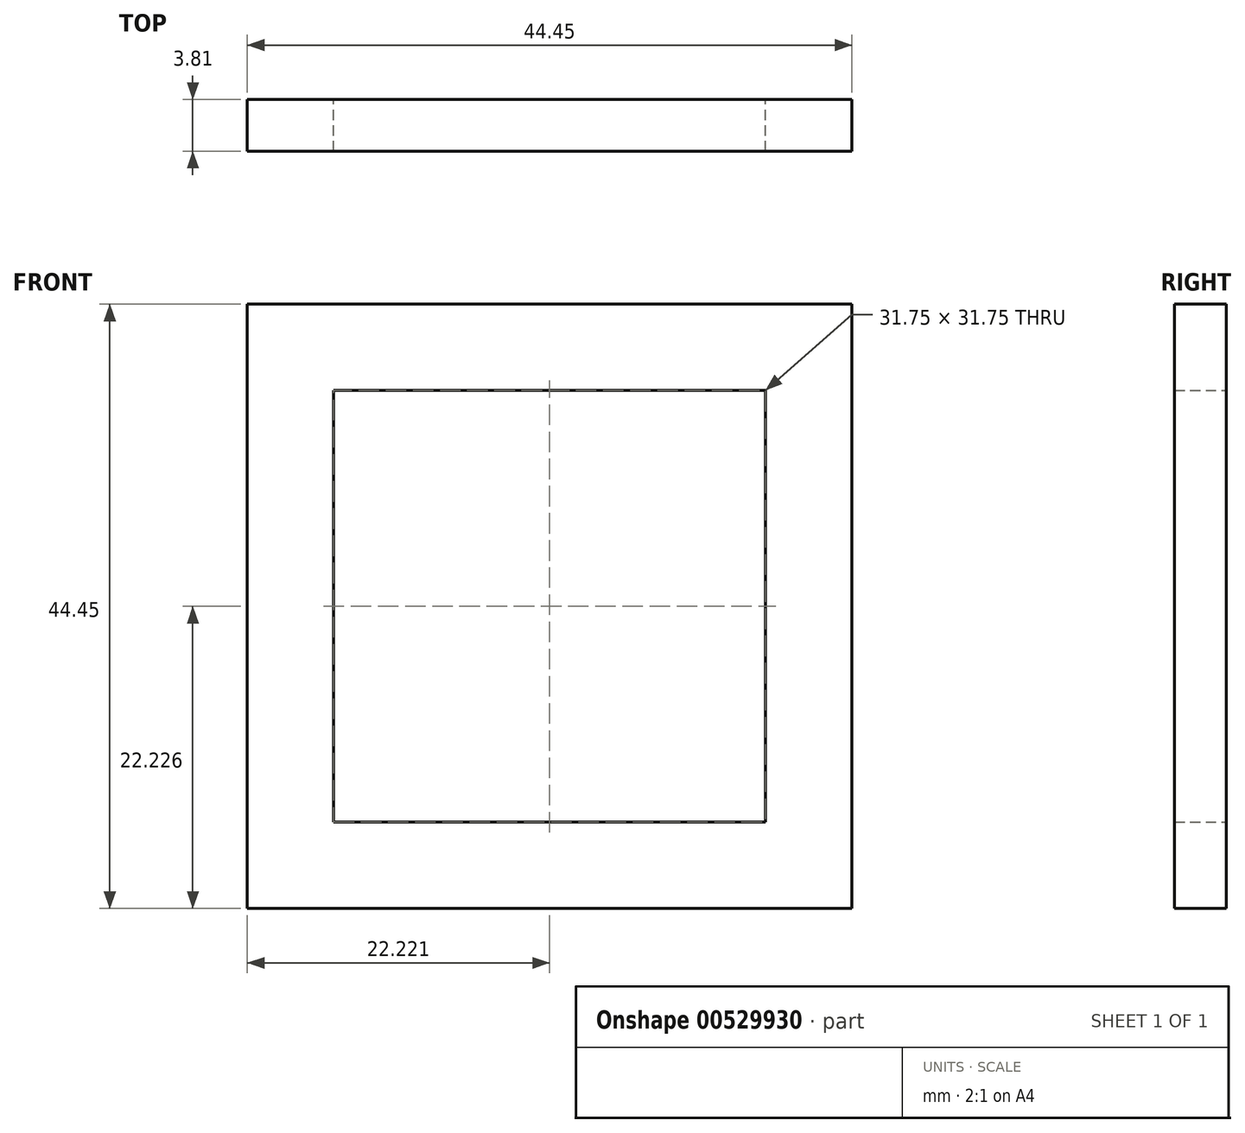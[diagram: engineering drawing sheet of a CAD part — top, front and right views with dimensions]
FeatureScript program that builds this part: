
annotation { "Feature Type Name" : "Feature", "Feature Type Description" : "" }
export const myFeature = defineFeature(function(context is Context, id is Id, definition is map)
    precondition{}
    {
        {
            var Q0;
            Q0=qCreatedBy(makeId("Front.planeOp"),FACE);
            var sketch = newSketch(context, id + "F0", { "sketchPlane" : qUnion([Q0])});
            skLineSegment(sketch, "E0.bottom", {"start": v(-21.7, 7.73) * mm, "end": v(22.75, 7.73) * mm});
            skLineSegment(sketch, "E0.top", {"start": v(-21.7, -36.72) * mm, "end": v(22.75, -36.72) * mm});
            skLineSegment(sketch, "E0.left", {"start": v(-21.7, 7.73) * mm, "end": v(-21.7, -36.72) * mm});
            skLineSegment(sketch, "E0.right", {"start": v(22.75, 7.73) * mm, "end": v(22.75, -36.72) * mm});
            skLineSegment(sketch, "E1.0", {"start": v(-15.35, 1.38) * mm, "end": v(-15.35, -30.37) * mm});
            skLineSegment(sketch, "E2.0", {"start": v(-15.35, -30.37) * mm, "end": v(16.4, -30.37) * mm});
            skLineSegment(sketch, "E3.0", {"start": v(16.4, 1.38) * mm, "end": v(16.4, -30.37) * mm});
            skLineSegment(sketch, "E4.0", {"start": v(-15.35, 1.38) * mm, "end": v(16.4, 1.38) * mm});
            skSolve(sketch);
        }
        {
            var Q0;
            Q0 = qSketchRegion(id + "F0", true);
            extrude(context, id + "F1", {"entities" : qUnion([Q0]), "depth" : 3.8 * mm, "offsetDistance" : 25.4 * mm});
        }
    });
